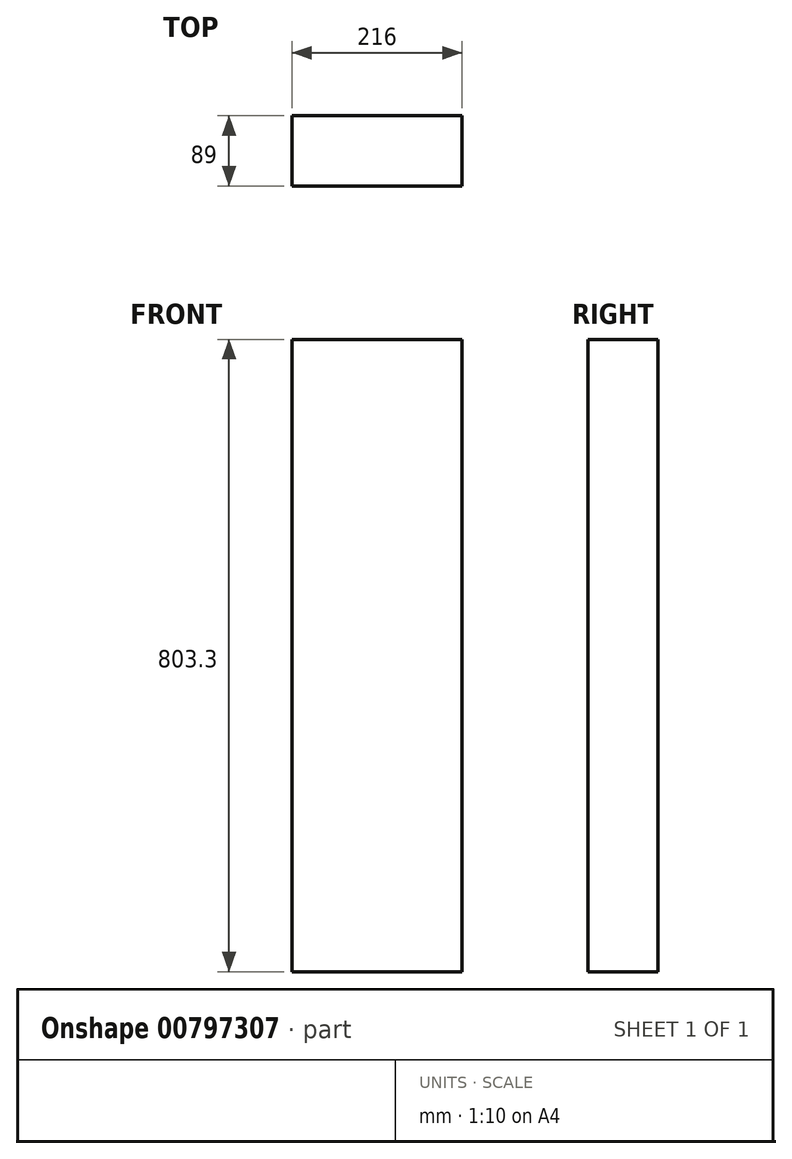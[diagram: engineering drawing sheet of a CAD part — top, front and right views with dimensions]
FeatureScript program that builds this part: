
annotation { "Feature Type Name" : "Feature", "Feature Type Description" : "" }
export const myFeature = defineFeature(function(context is Context, id is Id, definition is map)
    precondition{}
    {
        {
            var Q0;
            Q0=qCreatedBy(makeId("Front.planeOp"),FACE);
            var sketch = newSketch(context, id + "F0", { "sketchPlane" : qUnion([Q0])});
            skLineSegment(sketch, "E0.bottom", {"start": v(108, 401.65) * mm, "end": v(-108, 401.65) * mm});
            skLineSegment(sketch, "E0.top", {"start": v(108, -401.65) * mm, "end": v(-108, -401.65) * mm});
            skLineSegment(sketch, "E0.left", {"start": v(108, 401.65) * mm, "end": v(108, -401.65) * mm});
            skLineSegment(sketch, "E0.right", {"start": v(-108, 401.65) * mm, "end": v(-108, -401.65) * mm});
            skPoint(sketch, "E0.middle", {"position": v(0, 0) * mm});
            skSolve(sketch);
        }
        {
            var Q0;
            Q0=qSketchRegion(id+"F0",true);
            extrude(context, id + "F1", {"entities" : qUnion([Q0]), "depth" : 89 * mm, "offsetDistance" : 25 * mm, "symmetric" : true});
        }
    });
